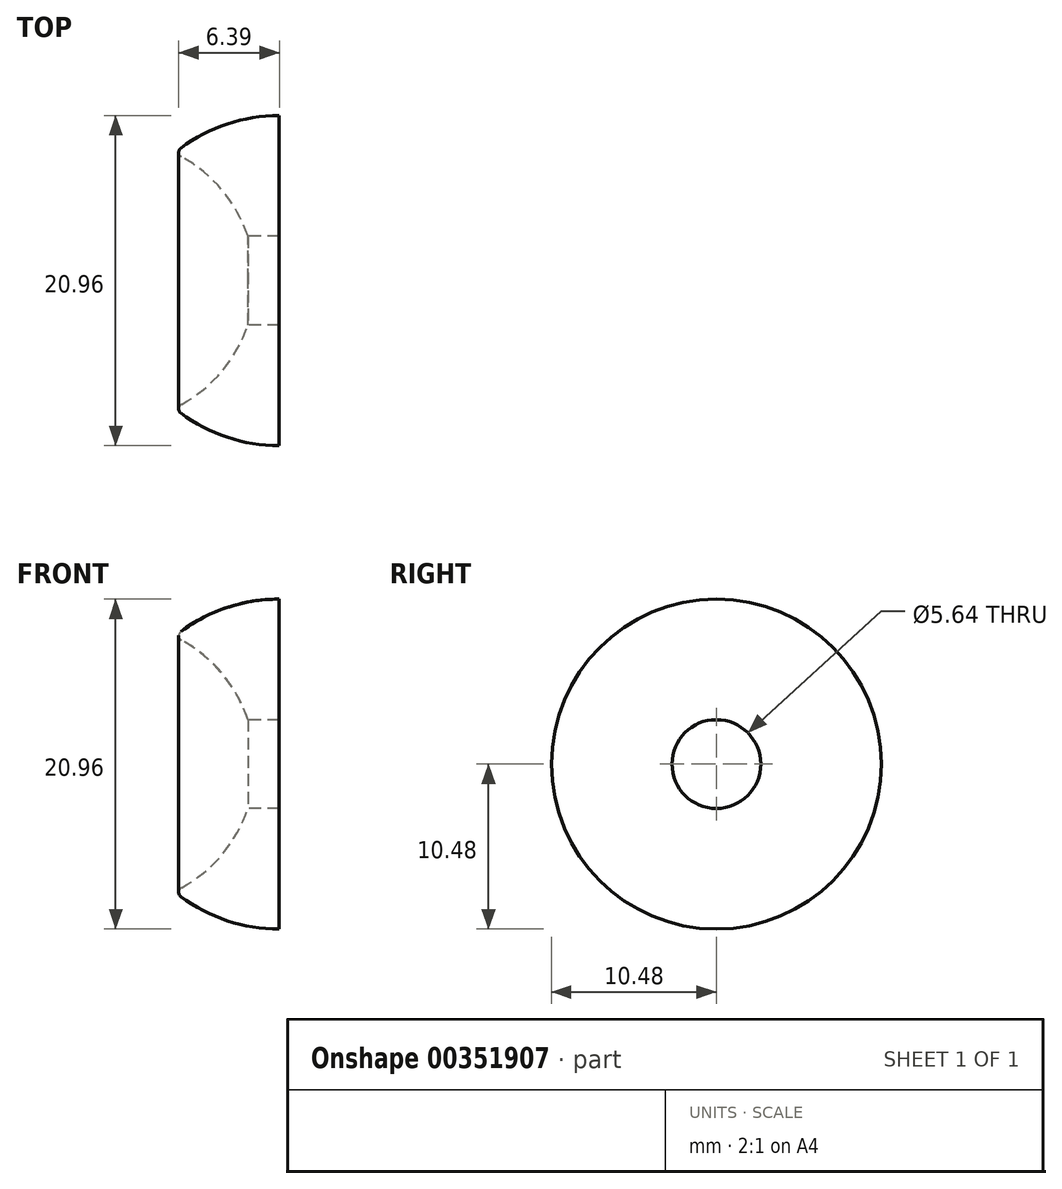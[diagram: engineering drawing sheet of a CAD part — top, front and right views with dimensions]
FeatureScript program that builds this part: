
annotation { "Feature Type Name" : "Feature", "Feature Type Description" : "" }
export const myFeature = defineFeature(function(context is Context, id is Id, definition is map)
    precondition{}
    {
        {
            var Q0;
            Q0=qCreatedBy(makeId("Front.planeOp"),FACE);
            var sketch = newSketch(context, id + "F0", { "sketchPlane" : qUnion([Q0])});
            skArc(sketch, "E0", {"start": v(-6.13, -8.5) * mm, "mid": v(0.04, -10.48) * mm, "end": v(6.2, -8.45) * mm});
            skArc(sketch, "E1", {"start": v(-6.15, -7.84) * mm, "mid": v(-1.52, 0.03) * mm, "end": v(-6.2, 7.86) * mm});
            skArc(sketch, "E2", {"start": v(6.06, 7.79) * mm, "mid": v(1.52, -0.02) * mm, "end": v(6.1, -7.8) * mm});
            skArc(sketch, "E3", {"start": v(-6.24, 8.42) * mm, "mid": v(-6.37, 8.13) * mm, "end": v(-6.2, 7.86) * mm});
            skArc(sketch, "E4.trimOffspring", {"start": v(6.24, 8.42) * mm, "mid": v(0, 10.48) * mm, "end": v(-6.24, 8.42) * mm});
            skArc(sketch, "E5.MirrorC", {"start": v(6.24, 8.42) * mm, "mid": v(6.44, 8.02) * mm, "end": v(6.06, 7.79) * mm});
            skArc(sketch, "E6.MirrorC", {"start": v(6.2, -8.45) * mm, "mid": v(6.41, -8.08) * mm, "end": v(6.1, -7.8) * mm});
            skArc(sketch, "E7.MirrorC", {"start": v(-6.13, -8.5) * mm, "mid": v(-6.44, -8.17) * mm, "end": v(-6.15, -7.84) * mm});
            skLineSegment(sketch, "E8", {"start": v(-1.52, 0) * mm, "end": v(1.52, 0) * mm});
            skLineSegment(sketch, "E9", {"start": v(0, 10.48) * mm, "end": v(0.04, -10.48) * mm});
            skLineSegment(sketch, "E10", {"start": v(1.98, 2.82) * mm, "end": v(-1.98, 2.82) * mm});
            skLineSegment(sketch, "E11", {"start": v(1.98, -2.82) * mm, "end": v(-1.98, -2.82) * mm});
            skPoint(sketch, "E12.MirrorCS.end.orphan", {"position": v(3.5, 2.82) * mm});
            skPoint(sketch, "E12.MirrorCS.start.orphan", {"position": v(10.52, 0.04) * mm});
            skPoint(sketch, "E13.MirrorCS.end.orphan", {"position": v(3.5, -2.82) * mm});
            skPoint(sketch, "E13.MirrorCS.start.orphan", {"position": v(3.5, 0) * mm});
            skSolve(sketch);
        }
        {
            var Q0;
            {var subQ0=sQuery(id+"F0.wireOp",EDGE,"E3");Q0=makeQuery(id+"F0.imprint","IMPRINT",FACE,{"disambiguationData":[TD([[makeQuery(id+"F0.imprint","IMPRINT",EDGE,{"derivedFrom":subQ0}),1.0]])]});}
            var Q1;
            {var subQ5=sQuery(id+"F0.wireOp",EDGE,"E5.MirrorC");Q1=makeQuery(id+"F0.imprint","IMPRINT",FACE,{"disambiguationData":[TD([[makeQuery(id+"F0.imprint","IMPRINT",EDGE,{"derivedFrom":subQ5}),-1.0]])]});}
            var Q2;
            Q2=sQuery(id+"F0.wireOp",EDGE,"E8");
            revolve(context, id + "F1", {"entities" : qUnion([Q0, Q1]), "axis" : qUnion([Q2]), "revolveType" : RevolveType.FULL});
        }
    });
